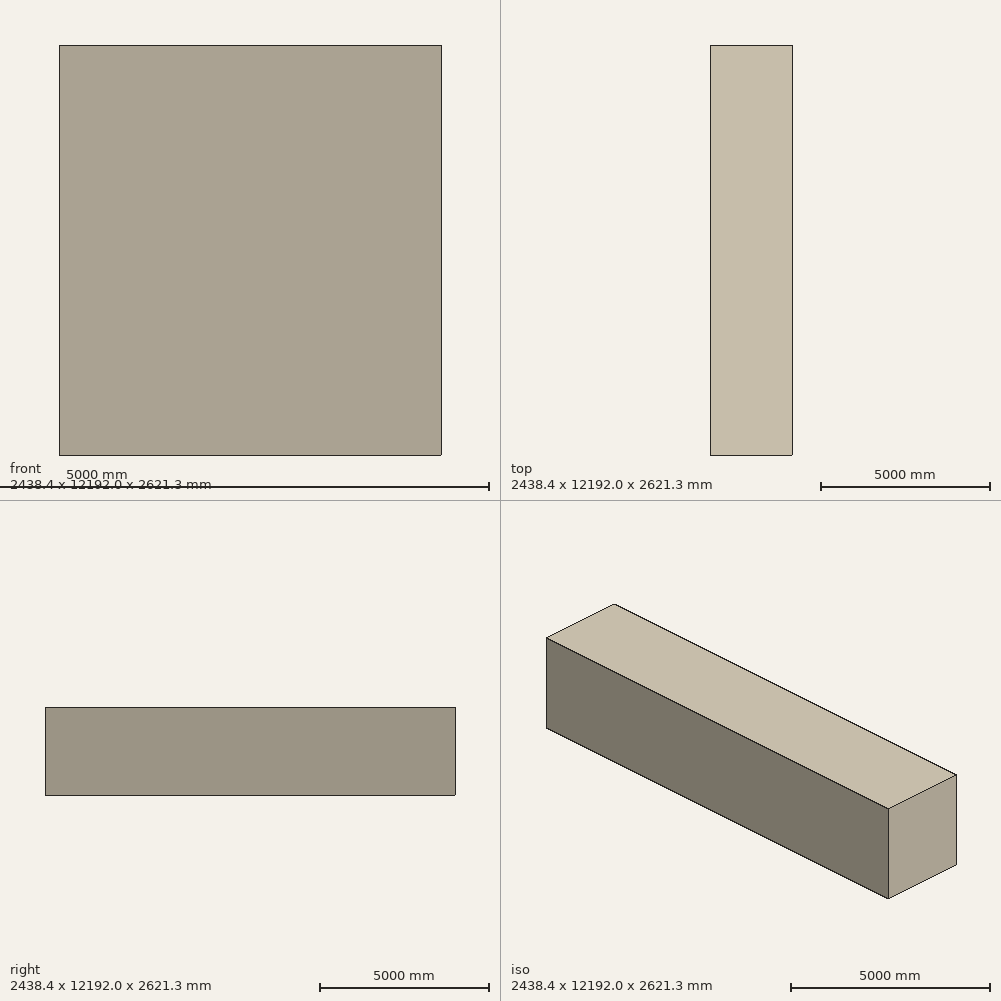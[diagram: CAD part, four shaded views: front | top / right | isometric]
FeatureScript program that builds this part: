
annotation { "Feature Type Name" : "Feature", "Feature Type Description" : "" }
export const myFeature = defineFeature(function(context is Context, id is Id, definition is map)
    precondition{}
    {
        {
            var Q0;
            Q0=qCreatedBy(makeId("Top.planeOp"),FACE);
            var sketch = newSketch(context, id + "F0", { "sketchPlane" : qUnion([Q0])});
            skLineSegment(sketch, "E0.bottom", {"start": v(-6079.69, 6089.03) * mm, "end": v(-3641.29, 6089.03) * mm});
            skLineSegment(sketch, "E0.top", {"start": v(-6079.69, -6102.97) * mm, "end": v(-3641.29, -6102.97) * mm});
            skLineSegment(sketch, "E0.left", {"start": v(-6079.69, 6089.03) * mm, "end": v(-6079.69, -6102.97) * mm});
            skLineSegment(sketch, "E0.right", {"start": v(-3641.29, 6089.03) * mm, "end": v(-3641.29, -6102.97) * mm});
            skSolve(sketch);
        }
        {
            var Q0;
            Q0=makeQuery(id+"F0.imprint","IMPRINT",FACE,{"disambiguationData":[TD([[makeQuery(id+"F0.imprint","IMPRINT",EDGE,{"derivedFrom":sQuery(id+"F0.wireOp",EDGE,"E0.bottom")}),-1.0]])]});
            extrude(context, id + "F1", {"entities" : qUnion([Q0]), "depth" : 2621.28 * mm});
        }
    });
